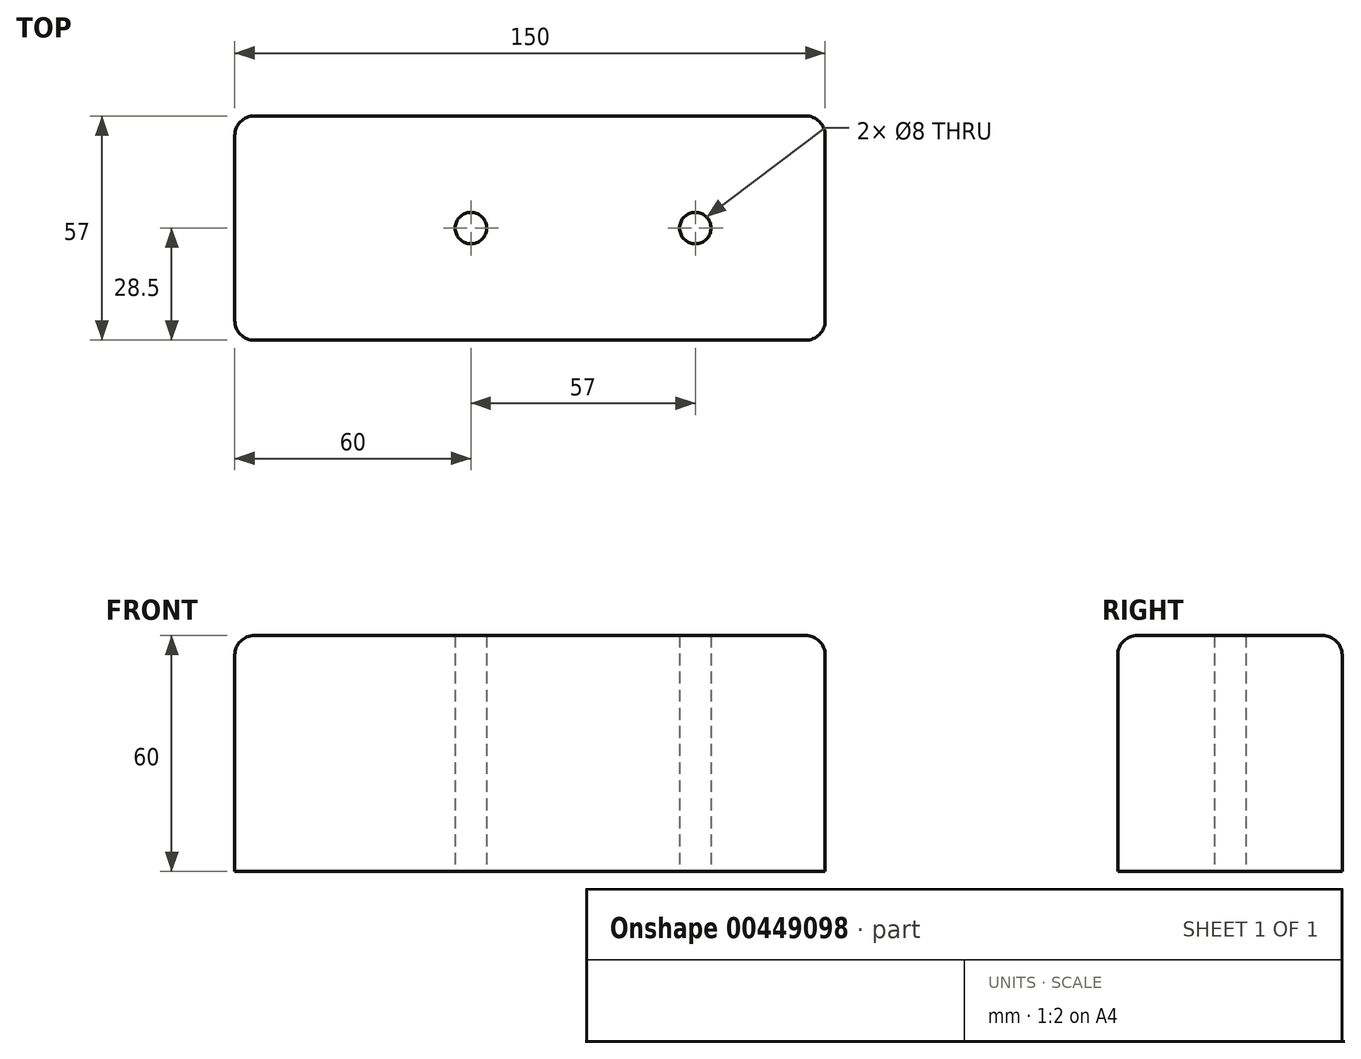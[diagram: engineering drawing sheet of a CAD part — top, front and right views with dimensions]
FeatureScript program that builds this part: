
annotation { "Feature Type Name" : "Feature", "Feature Type Description" : "" }
export const myFeature = defineFeature(function(context is Context, id is Id, definition is map)
    precondition{}
    {
        {
            var Q0;
            Q0=qCreatedBy(makeId("Top.planeOp"),FACE);
            var sketch = newSketch(context, id + "F0", { "sketchPlane" : qUnion([Q0])});
            skLineSegment(sketch, "E0.bottom", {"start": v(0, 0) * mm, "end": v(150, 0) * mm});
            skLineSegment(sketch, "E0.top", {"start": v(0, 57) * mm, "end": v(150, 57) * mm});
            skLineSegment(sketch, "E0.left", {"start": v(0, 0) * mm, "end": v(0, 57) * mm});
            skLineSegment(sketch, "E0.right", {"start": v(150, 0) * mm, "end": v(150, 57) * mm});
            skCircle(sketch, "E1", {"center": v(60, 28.5) * mm, "radius": 4 * mm});
            skCircle(sketch, "E2", {"center": v(117, 28.5) * mm, "radius": 4 * mm});
            skSolve(sketch);
        }
        {
            var Q0;
            Q0=makeQuery(id+"F0.imprint","IMPRINT",FACE,{"disambiguationData":[TD([[makeQuery(id+"F0.imprint","IMPRINT",EDGE,{"derivedFrom":sQuery(id+"F0.wireOp",EDGE,"E0.bottom")}),1.0]])]});
            extrude(context, id + "F1", {"entities" : qUnion([Q0]), "depth" : 60 * mm});
        }
        {
            var Q0;
            Q0=makeQuery(id+"F1.opExtrude","CAP_EDGE",EDGE,{"disambiguationData":[OSD([sQuery(id+"F0.wireOp",EDGE,"E0.bottom")])],"isStart":false});
            var Q1;
            Q1=makeQuery(id+"F1.opExtrude","SWEPT_EDGE",EDGE,{"disambiguationData":[OSD([sQuery(id+"F0.wireOp",EDGE,"E0.bottom"),sQuery(id+"F0.wireOp",EDGE,"E0.right")])]});
            var Q2;
            Q2=makeQuery(id+"F1.opExtrude","CAP_EDGE",EDGE,{"disambiguationData":[OSD([sQuery(id+"F0.wireOp",EDGE,"E0.right")])],"isStart":false});
            var Q3;
            Q3=makeQuery(id+"F1.opExtrude","SWEPT_EDGE",EDGE,{"disambiguationData":[OSD([sQuery(id+"F0.wireOp",EDGE,"E0.top"),sQuery(id+"F0.wireOp",EDGE,"E0.right")])]});
            var Q4;
            Q4=makeQuery(id+"F1.opExtrude","CAP_EDGE",EDGE,{"disambiguationData":[OSD([sQuery(id+"F0.wireOp",EDGE,"E0.top")])],"isStart":false});
            var Q5;
            Q5=makeQuery(id+"F1.opExtrude","SWEPT_EDGE",EDGE,{"disambiguationData":[OSD([sQuery(id+"F0.wireOp",EDGE,"E0.top"),sQuery(id+"F0.wireOp",EDGE,"E0.left")])]});
            var Q6;
            Q6=makeQuery(id+"F1.opExtrude","CAP_EDGE",EDGE,{"disambiguationData":[OSD([sQuery(id+"F0.wireOp",EDGE,"E0.left")])],"isStart":false});
            var Q7;
            Q7=makeQuery(id+"F1.opExtrude","SWEPT_EDGE",EDGE,{"disambiguationData":[OSD([sQuery(id+"F0.wireOp",EDGE,"E0.bottom"),sQuery(id+"F0.wireOp",EDGE,"E0.left")])]});
            fillet(context, id + "F2", {"entities" : qUnion([Q0, Q1, Q2, Q3, Q4, Q5, Q6, Q7]), "radius" : 5 * mm, "tangentPropagation" : true, "allowEdgeOverflow" : false});
        }
    });
